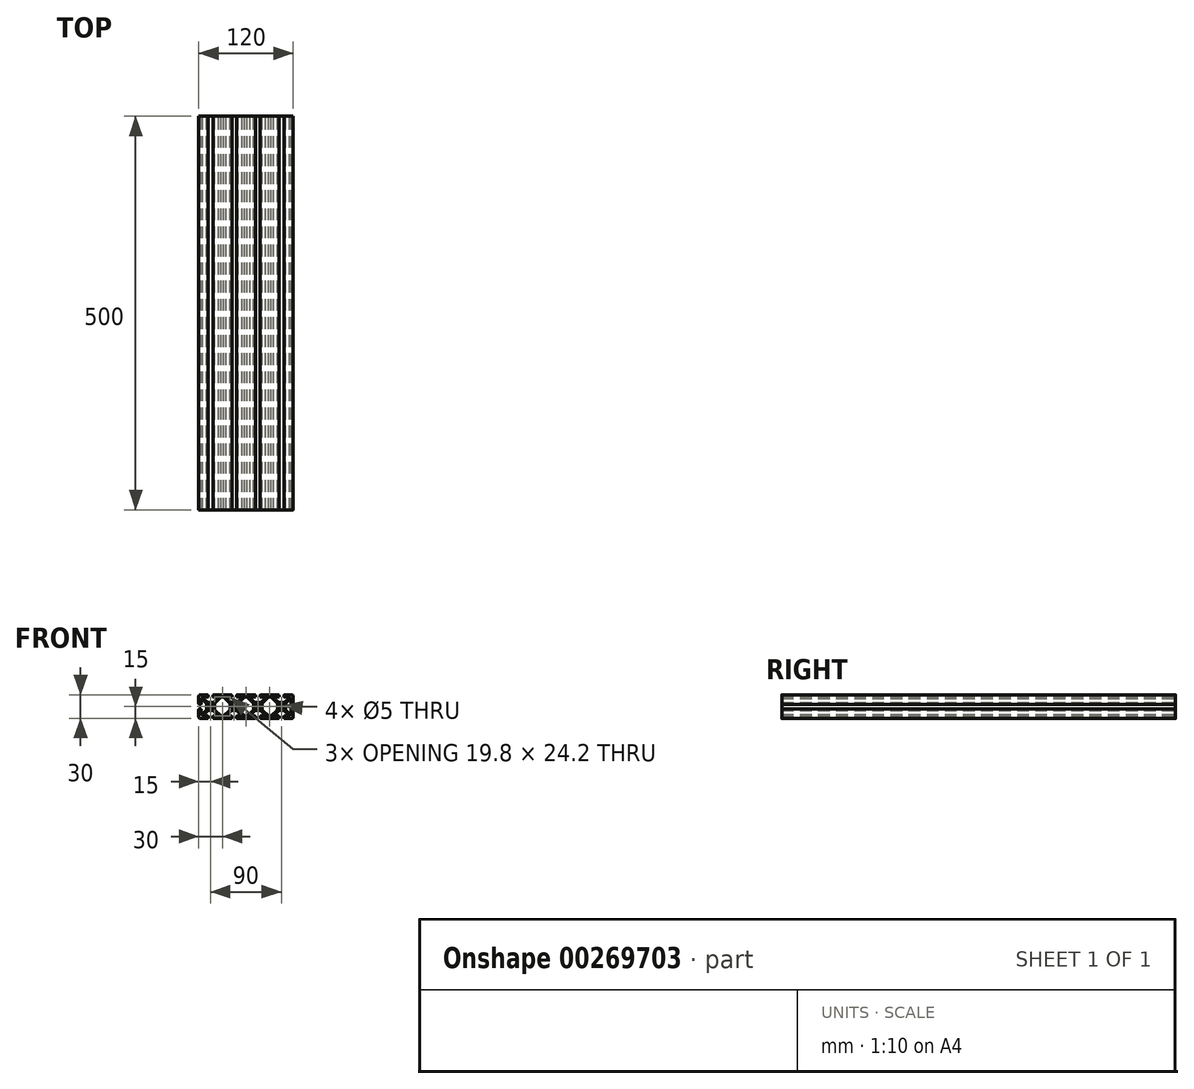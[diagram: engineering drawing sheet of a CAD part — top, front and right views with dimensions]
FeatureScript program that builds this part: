
annotation { "Feature Type Name" : "Feature", "Feature Type Description" : "" }
export const myFeature = defineFeature(function(context is Context, id is Id, definition is map)
    precondition{}
    {
        {
            var Q0;
            Q0=qCreatedBy(makeId("Front.planeOp"),FACE);
            var sketch = newSketch(context, id + "F0", { "sketchPlane" : qUnion([Q0])});
            skLineSegment(sketch, "E0.top", {"start": v(-58.2, -15) * mm, "end": v(-49, -15) * mm});
            skCircle(sketch, "E1", {"center": v(-45, 0) * mm, "radius": 2.5 * mm});
            skCircle(sketch, "E2", {"center": v(-15, 0) * mm, "radius": 2.5 * mm});
            skPoint(sketch, "E3", {"position": v(0, 10) * mm});
            skLineSegment(sketch, "E4", {"start": v(-45, 0) * mm, "end": v(-15, 0) * mm, "construction": true});
            skLineSegment(sketch, "E5", {"start": v(-15, 0) * mm, "end": v(0, 0) * mm, "construction": true});
            skPoint(sketch, "E6", {"position": v(0, 0) * mm});
            skLineSegment(sketch, "E7", {"start": v(-54.62, -12.1) * mm, "end": v(-48.5, -12.1) * mm});
            skLineSegment(sketch, "E8", {"start": v(-45, 0) * mm, "end": v(-45, -15) * mm, "construction": true});
            skLineSegment(sketch, "E9.bottom", {"start": v(-42.2, -5.1) * mm, "end": v(-47.8, -5.1) * mm});
            skLineSegment(sketch, "E10.trimOffspring", {"start": v(-48, -12.6) * mm, "end": v(-48, -14) * mm});
            skLineSegment(sketch, "E11.trimOffspring", {"start": v(-42, -12.6) * mm, "end": v(-42, -14) * mm});
            skLineSegment(sketch, "E12.trimOffspring", {"start": v(-41.5, -12.1) * mm, "end": v(-35.38, -12.1) * mm});
            skLineSegment(sketch, "E13.0", {"start": v(-56.25, -9.97) * mm, "end": v(-50.83, -4.56) * mm});
            skLineSegment(sketch, "E14.trimOffspring", {"start": v(-54.97, -11.25) * mm, "end": v(-49.56, -5.83) * mm});
            skLineSegment(sketch, "E15", {"start": v(-45, 0) * mm, "end": v(-60, -15) * mm, "construction": true});
            skLineSegment(sketch, "E16.MirrorCS", {"start": v(-57.1, -9.62) * mm, "end": v(-57.1, -3.5) * mm});
            skLineSegment(sketch, "E17.MirrorCS", {"start": v(-57.6, -3) * mm, "end": v(-59, -3) * mm});
            skLineSegment(sketch, "E18.MirrorCS", {"start": v(-35.03, -11.25) * mm, "end": v(-40.44, -5.83) * mm});
            skLineSegment(sketch, "E19.MirrorCS", {"start": v(-31.63, -12.1) * mm, "end": v(-39.17, -4.56) * mm});
            skLineSegment(sketch, "E20.trimOffspring", {"start": v(-60, -4) * mm, "end": v(-60, -13.2) * mm});
            skPoint(sketch, "E21.visualSharp", {"position": v(-60, -15) * mm});
            skArc(sketch, "E21.filletArc", {"start": v(-60, -13.2) * mm, "mid": v(-59.47, -14.47) * mm, "end": v(-58.2, -15) * mm});
            skPoint(sketch, "E22.visualSharp", {"position": v(-48, -15) * mm});
            skArc(sketch, "E22.filletArc", {"start": v(-49, -15) * mm, "mid": v(-48.3, -14.7) * mm, "end": v(-48, -14) * mm});
            skLineSegment(sketch, "E23", {"start": v(-48, -14) * mm, "end": v(-42, -14) * mm, "construction": true});
            skPoint(sketch, "E24", {"position": v(-45, -14) * mm});
            skPoint(sketch, "E25.orphan", {"position": v(-34.33, -5.1) * mm});
            skPoint(sketch, "E26.orphan", {"position": v(-45.67, -5.1) * mm});
            skPoint(sketch, "E27.visualSharp", {"position": v(-48.83, -5.1) * mm});
            skArc(sketch, "E27.filletArc", {"start": v(-47.8, -5.1) * mm, "mid": v(-48.75, -5.3) * mm, "end": v(-49.56, -5.83) * mm});
            skPoint(sketch, "E28.visualSharp", {"position": v(-41.17, -5.1) * mm});
            skArc(sketch, "E28.filletArc", {"start": v(-40.44, -5.83) * mm, "mid": v(-41.25, -5.3) * mm, "end": v(-42.2, -5.1) * mm});
            skPoint(sketch, "E29.visualSharp", {"position": v(-41.12, 5.15) * mm});
            skArc(sketch, "E29.filletArc", {"start": v(-50.83, -4.56) * mm, "mid": v(-50.3, -3.75) * mm, "end": v(-50.1, -2.8) * mm});
            skPoint(sketch, "E30.visualSharp", {"position": v(-48.88, 5.15) * mm});
            skPoint(sketch, "E31.visualSharp", {"position": v(-42, -15) * mm});
            skArc(sketch, "E31.filletArc", {"start": v(-42, -14) * mm, "mid": v(-41.7, -14.7) * mm, "end": v(-41, -15) * mm});
            skPoint(sketch, "E32.visualSharp", {"position": v(-42, -12.1) * mm});
            skArc(sketch, "E32.filletArc", {"start": v(-41.5, -12.1) * mm, "mid": v(-41.85, -12.25) * mm, "end": v(-42, -12.6) * mm});
            skPoint(sketch, "E33.visualSharp", {"position": v(-48, -12.1) * mm});
            skArc(sketch, "E33.filletArc", {"start": v(-48, -12.6) * mm, "mid": v(-48.15, -12.25) * mm, "end": v(-48.5, -12.1) * mm});
            skPoint(sketch, "E34.visualSharp", {"position": v(-57.1, -3) * mm});
            skArc(sketch, "E34.filletArc", {"start": v(-57.1, -3.5) * mm, "mid": v(-57.25, -3.15) * mm, "end": v(-57.6, -3) * mm});
            skPoint(sketch, "E35.visualSharp", {"position": v(-60, -3) * mm});
            skArc(sketch, "E35.filletArc", {"start": v(-59, -3) * mm, "mid": v(-59.7, -3.3) * mm, "end": v(-60, -4) * mm});
            skPoint(sketch, "E36.visualSharp", {"position": v(-57.1, -10.83) * mm});
            skArc(sketch, "E36.filletArc", {"start": v(-57.1, -9.62) * mm, "mid": v(-56.8, -10.08) * mm, "end": v(-56.25, -9.97) * mm});
            skPoint(sketch, "E37.visualSharp", {"position": v(-55.83, -12.1) * mm});
            skArc(sketch, "E37.filletArc", {"start": v(-54.97, -11.25) * mm, "mid": v(-55.08, -11.8) * mm, "end": v(-54.62, -12.1) * mm});
            skPoint(sketch, "E38.visualSharp", {"position": v(-34.17, -12.1) * mm});
            skArc(sketch, "E38.filletArc", {"start": v(-35.38, -12.1) * mm, "mid": v(-34.92, -11.8) * mm, "end": v(-35.03, -11.25) * mm});
            skLineSegment(sketch, "E39", {"start": v(-43.9, 2.36) * mm, "end": v(-42.64, 1.1) * mm, "construction": true});
            skPoint(sketch, "E40", {"position": v(-43.27, 1.73) * mm});
            skLineSegment(sketch, "E41.MirrorCS", {"start": v(-58.2, 15) * mm, "end": v(-49, 15) * mm});
            skArc(sketch, "E42.MirrorCS", {"start": v(-60, 13.2) * mm, "mid": v(-59.47, 14.47) * mm, "end": v(-58.2, 15) * mm});
            skLineSegment(sketch, "E43.MirrorCS", {"start": v(-60, 4) * mm, "end": v(-60, 13.2) * mm});
            skArc(sketch, "E44.MirrorCS", {"start": v(-59, 3) * mm, "mid": v(-59.7, 3.3) * mm, "end": v(-60, 4) * mm});
            skLineSegment(sketch, "E45.MirrorCS", {"start": v(-57.6, 3) * mm, "end": v(-59, 3) * mm});
            skArc(sketch, "E46.MirrorCS", {"start": v(-57.1, 3.5) * mm, "mid": v(-57.25, 3.15) * mm, "end": v(-57.6, 3) * mm});
            skLineSegment(sketch, "E47.MirrorCS", {"start": v(-57.1, 9.62) * mm, "end": v(-57.1, 3.5) * mm});
            skArc(sketch, "E48.MirrorCS", {"start": v(-57.1, 9.62) * mm, "mid": v(-56.8, 10.08) * mm, "end": v(-56.25, 9.97) * mm});
            skLineSegment(sketch, "E49.MirrorCS", {"start": v(-56.25, 9.97) * mm, "end": v(-50.83, 4.56) * mm});
            skArc(sketch, "E50.MirrorCS", {"start": v(-50.83, 4.56) * mm, "mid": v(-50.3, 3.75) * mm, "end": v(-50.1, 2.8) * mm});
            skArc(sketch, "E51.MirrorCS", {"start": v(-49, 15) * mm, "mid": v(-48.3, 14.7) * mm, "end": v(-48, 14) * mm});
            skLineSegment(sketch, "E52.MirrorCS", {"start": v(-48, 12.6) * mm, "end": v(-48, 14) * mm});
            skArc(sketch, "E53.MirrorCS", {"start": v(-48, 12.6) * mm, "mid": v(-48.15, 12.25) * mm, "end": v(-48.5, 12.1) * mm});
            skLineSegment(sketch, "E54.MirrorCS", {"start": v(-54.62, 12.1) * mm, "end": v(-48.5, 12.1) * mm});
            skArc(sketch, "E55.MirrorCS", {"start": v(-54.97, 11.25) * mm, "mid": v(-55.08, 11.8) * mm, "end": v(-54.62, 12.1) * mm});
            skLineSegment(sketch, "E56.MirrorCS", {"start": v(-54.97, 11.25) * mm, "end": v(-49.56, 5.83) * mm});
            skArc(sketch, "E57.MirrorCS", {"start": v(-47.8, 5.1) * mm, "mid": v(-48.75, 5.3) * mm, "end": v(-49.56, 5.83) * mm});
            skLineSegment(sketch, "E58.MirrorCS", {"start": v(-42.2, 5.1) * mm, "end": v(-47.8, 5.1) * mm});
            skArc(sketch, "E59.MirrorCS", {"start": v(-40.44, 5.83) * mm, "mid": v(-41.25, 5.3) * mm, "end": v(-42.2, 5.1) * mm});
            skLineSegment(sketch, "E60.MirrorCS", {"start": v(-35.03, 11.25) * mm, "end": v(-40.44, 5.83) * mm});
            skArc(sketch, "E61.MirrorCS", {"start": v(-35.38, 12.1) * mm, "mid": v(-34.92, 11.8) * mm, "end": v(-35.03, 11.25) * mm});
            skLineSegment(sketch, "E62.MirrorCS", {"start": v(-41.5, 12.1) * mm, "end": v(-35.38, 12.1) * mm});
            skArc(sketch, "E63.MirrorCS", {"start": v(-41.5, 12.1) * mm, "mid": v(-41.85, 12.25) * mm, "end": v(-42, 12.6) * mm});
            skLineSegment(sketch, "E64.MirrorCS", {"start": v(-42, 12.6) * mm, "end": v(-42, 14) * mm});
            skArc(sketch, "E65.MirrorCS", {"start": v(-42, 14) * mm, "mid": v(-41.7, 14.7) * mm, "end": v(-41, 15) * mm});
            skLineSegment(sketch, "E66.MirrorCS", {"start": v(-31.63, 12.1) * mm, "end": v(-39.17, 4.56) * mm});
            skLineSegment(sketch, "E67", {"start": v(-50.1, -2.8) * mm, "end": v(-50.1, 2.8) * mm});
            skLineSegment(sketch, "E68", {"start": v(-39.9, 2.8) * mm, "end": v(-39.9, -2.8) * mm});
            skLineSegment(sketch, "E69", {"start": v(-30, 0) * mm, "end": v(-30, -12.6) * mm, "construction": true});
            skLineSegment(sketch, "E70.MirrorCS", {"start": v(-18, -12.6) * mm, "end": v(-18, -14) * mm});
            skArc(sketch, "E71.MirrorCS", {"start": v(-18.5, -12.1) * mm, "mid": v(-18.15, -12.25) * mm, "end": v(-18, -12.6) * mm});
            skPoint(sketch, "E72.MirrorP", {"position": v(-18, -15) * mm});
            skArc(sketch, "E73.MirrorCS", {"start": v(-18, -14) * mm, "mid": v(-18.3, -14.7) * mm, "end": v(-19, -15) * mm});
            skPoint(sketch, "E74.MirrorP", {"position": v(-18, -12.1) * mm});
            skLineSegment(sketch, "E75.MirrorCS", {"start": v(-18.5, -12.1) * mm, "end": v(-24.62, -12.1) * mm});
            skPoint(sketch, "E76.MirrorP", {"position": v(-25.83, -12.1) * mm});
            skPoint(sketch, "E77.MirrorP", {"position": v(-11.12, 5.15) * mm});
            skPoint(sketch, "E78.MirrorP", {"position": v(-14.33, -5.1) * mm});
            skPoint(sketch, "E79.MirrorP", {"position": v(-18.83, -5.1) * mm});
            skLineSegment(sketch, "E80.MirrorCS", {"start": v(-28.37, -12.1) * mm, "end": v(-20.83, -4.56) * mm});
            skLineSegment(sketch, "E81.MirrorCS", {"start": v(-18, 12.6) * mm, "end": v(-18, 14) * mm});
            skArc(sketch, "E82.MirrorCS", {"start": v(-18, 14) * mm, "mid": v(-18.3, 14.7) * mm, "end": v(-19, 15) * mm});
            skLineSegment(sketch, "E83.MirrorCS", {"start": v(-24.97, 11.25) * mm, "end": v(-19.56, 5.83) * mm});
            skLineSegment(sketch, "E84.MirrorCS", {"start": v(-28.37, 12.1) * mm, "end": v(-20.83, 4.56) * mm});
            skLineSegment(sketch, "E85.MirrorCS", {"start": v(-18.5, 12.1) * mm, "end": v(-24.62, 12.1) * mm});
            skArc(sketch, "E86.MirrorCS", {"start": v(-18.5, 12.1) * mm, "mid": v(-18.15, 12.25) * mm, "end": v(-18, 12.6) * mm});
            skArc(sketch, "E87.MirrorCS", {"start": v(-24.62, 12.1) * mm, "mid": v(-25.08, 11.8) * mm, "end": v(-24.97, 11.25) * mm});
            skArc(sketch, "E88.MirrorCS", {"start": v(-19.56, 5.83) * mm, "mid": v(-18.75, 5.3) * mm, "end": v(-17.8, 5.1) * mm});
            skLineSegment(sketch, "E89.MirrorCS", {"start": v(-17.8, 5.1) * mm, "end": v(-12.2, 5.1) * mm});
            skArc(sketch, "E90.MirrorCS", {"start": v(-11, -15) * mm, "mid": v(-11.7, -14.7) * mm, "end": v(-12, -14) * mm});
            skLineSegment(sketch, "E91.MirrorCS", {"start": v(-12, -12.6) * mm, "end": v(-12, -14) * mm});
            skArc(sketch, "E92.MirrorCS", {"start": v(-12, -12.6) * mm, "mid": v(-11.85, -12.25) * mm, "end": v(-11.5, -12.1) * mm});
            skLineSegment(sketch, "E93.MirrorCS", {"start": v(-5.38, -12.1) * mm, "end": v(-11.5, -12.1) * mm});
            skPoint(sketch, "E94.visualSharp", {"position": v(-31.63, 12.1) * mm});
            skPoint(sketch, "E95.visualSharp", {"position": v(-28.37, 12.1) * mm});
            skPoint(sketch, "E96.visualSharp", {"position": v(-31.63, -12.1) * mm});
            skPoint(sketch, "E97.visualSharp", {"position": v(-28.37, -12.1) * mm});
            skArc(sketch, "E98.MirrorCS", {"start": v(-24.62, -12.1) * mm, "mid": v(-25.08, -11.8) * mm, "end": v(-24.97, -11.25) * mm});
            skLineSegment(sketch, "E99.MirrorCS", {"start": v(-24.97, -11.25) * mm, "end": v(-19.56, -5.83) * mm});
            skArc(sketch, "E100.MirrorCS", {"start": v(-19.56, -5.83) * mm, "mid": v(-18.75, -5.3) * mm, "end": v(-17.8, -5.1) * mm});
            skLineSegment(sketch, "E101.MirrorCS", {"start": v(-17.8, -5.1) * mm, "end": v(-12.2, -5.1) * mm});
            skArc(sketch, "E102.MirrorCS", {"start": v(-12.2, -5.1) * mm, "mid": v(-11.25, -5.3) * mm, "end": v(-10.44, -5.83) * mm});
            skLineSegment(sketch, "E103.MirrorCS", {"start": v(-5.03, -11.25) * mm, "end": v(-10.44, -5.83) * mm});
            skArc(sketch, "E104.MirrorCS", {"start": v(-5.03, -11.25) * mm, "mid": v(-4.92, -11.8) * mm, "end": v(-5.38, -12.1) * mm});
            skArc(sketch, "E105.MirrorCS", {"start": v(-12.2, 5.1) * mm, "mid": v(-11.25, 5.3) * mm, "end": v(-10.44, 5.83) * mm});
            skLineSegment(sketch, "E106.MirrorCS", {"start": v(-5.03, 11.25) * mm, "end": v(-10.44, 5.83) * mm});
            skArc(sketch, "E107.MirrorCS", {"start": v(-5.03, 11.25) * mm, "mid": v(-4.92, 11.8) * mm, "end": v(-5.38, 12.1) * mm});
            skLineSegment(sketch, "E108.MirrorCS", {"start": v(-5.38, 12.1) * mm, "end": v(-11.5, 12.1) * mm});
            skArc(sketch, "E109.MirrorCS", {"start": v(-12, 12.6) * mm, "mid": v(-11.85, 12.25) * mm, "end": v(-11.5, 12.1) * mm});
            skLineSegment(sketch, "E110.MirrorCS", {"start": v(-12, 12.6) * mm, "end": v(-12, 14) * mm});
            skArc(sketch, "E111.MirrorCS", {"start": v(-11, 15) * mm, "mid": v(-11.7, 14.7) * mm, "end": v(-12, 14) * mm});
            skArc(sketch, "E112.MirrorCS", {"start": v(-9.17, -4.56) * mm, "mid": v(-9.7, -3.75) * mm, "end": v(-9.9, -2.8) * mm});
            skLineSegment(sketch, "E113.MirrorCS", {"start": v(-9.9, -2.8) * mm, "end": v(-9.9, 2.8) * mm});
            skArc(sketch, "E114.MirrorCS", {"start": v(-9.17, 4.56) * mm, "mid": v(-9.7, 3.75) * mm, "end": v(-9.9, 2.8) * mm});
            skLineSegment(sketch, "E115", {"start": v(-15, 0) * mm, "end": v(-15, -13.35) * mm, "construction": true});
            skLineSegment(sketch, "E116", {"start": v(-41, -15) * mm, "end": v(-30, -15) * mm});
            skLineSegment(sketch, "E117", {"start": v(-30, -15) * mm, "end": v(-19, -15) * mm});
            skLineSegment(sketch, "E118.MirrorCS", {"start": v(-30, 15) * mm, "end": v(-19, 15) * mm});
            skLineSegment(sketch, "E119.MirrorCS", {"start": v(-41, 15) * mm, "end": v(-30, 15) * mm});
            skLineSegment(sketch, "E120.MirrorCS", {"start": v(0, -15) * mm, "end": v(-11, -15) * mm});
            skLineSegment(sketch, "E121.MirrorCS", {"start": v(-1.63, -12.1) * mm, "end": v(-9.9, -3.83) * mm});
            skLineSegment(sketch, "E122.MirrorCS", {"start": v(0, -12.1) * mm, "end": v(-1.63, -12.1) * mm});
            skLineSegment(sketch, "E123.MirrorCS", {"start": v(0, 15) * mm, "end": v(-11, 15) * mm});
            skLineSegment(sketch, "E124.MirrorCS", {"start": v(-1.63, 12.1) * mm, "end": v(-9.9, 3.83) * mm});
            skLineSegment(sketch, "E125", {"start": v(0, 10) * mm, "end": v(0, -15) * mm, "construction": true});
            skPoint(sketch, "E126.orphan", {"position": v(15, 0) * mm});
            skLineSegment(sketch, "E127", {"start": v(0, -15) * mm, "end": v(0, -12.1) * mm});
            skLineSegment(sketch, "E128", {"start": v(0, 15) * mm, "end": v(0, 12.1) * mm});
            skLineSegment(sketch, "E129", {"start": v(-31.63, 12.1) * mm, "end": v(-28.37, 12.1) * mm});
            skLineSegment(sketch, "E130", {"start": v(-31.63, -12.1) * mm, "end": v(-28.37, -12.1) * mm});
            skLineSegment(sketch, "E131", {"start": v(-1.63, 12.1) * mm, "end": v(0, 12.1) * mm});
            skPoint(sketch, "E132.visualSharp", {"position": v(-39.9, 3.83) * mm});
            skArc(sketch, "E132.filletArc", {"start": v(-39.17, 4.56) * mm, "mid": v(-39.7, 3.75) * mm, "end": v(-39.9, 2.8) * mm});
            skPoint(sketch, "E133.visualSharp", {"position": v(-39.9, -3.83) * mm});
            skArc(sketch, "E133.filletArc", {"start": v(-39.9, -2.8) * mm, "mid": v(-39.7, -3.75) * mm, "end": v(-39.17, -4.56) * mm});
            skPoint(sketch, "E134.visualSharp", {"position": v(-20.1, 3.83) * mm});
            skArc(sketch, "E134.filletArc", {"start": v(-20.1, 2.8) * mm, "mid": v(-20.3, 3.75) * mm, "end": v(-20.83, 4.56) * mm});
            skLineSegment(sketch, "E135", {"start": v(-20.1, 2.8) * mm, "end": v(-20.1, -2.8) * mm});
            skPoint(sketch, "E136.visualSharp", {"position": v(-20.1, -3.83) * mm});
            skArc(sketch, "E136.filletArc", {"start": v(-20.83, -4.56) * mm, "mid": v(-20.3, -3.75) * mm, "end": v(-20.1, -2.8) * mm});
            skSolve(sketch);
        }
        {
            var Q0;
            Q0=makeQuery(id+"F0.imprint","IMPRINT",FACE,{"disambiguationData":[TD([[makeQuery(id+"F0.imprint","IMPRINT",EDGE,{"derivedFrom":sQuery(id+"F0.wireOp",EDGE,"E0.top")}),1.0]])]});
            extrude(context, id + "F1", {"entities" : qUnion([Q0]), "depth" : 500 * mm});
        }
        {
            var Q0;
            Q0=makeQuery(id+"F1.opExtrude","SWEPT_BODY",BODY,{"disambiguationData":[OSD([sQuery(id+"F0.wireOp",EDGE,"E0.top"),sQuery(id+"F0.wireOp",EDGE,"E1"),sQuery(id+"F0.wireOp",EDGE,"E2"),sQuery(id+"F0.wireOp",EDGE,"E7"),sQuery(id+"F0.wireOp",EDGE,"E9.bottom"),sQuery(id+"F0.wireOp",EDGE,"E10.trimOffspring"),sQuery(id+"F0.wireOp",EDGE,"E11.trimOffspring"),sQuery(id+"F0.wireOp",EDGE,"E12.trimOffspring"),sQuery(id+"F0.wireOp",EDGE,"E13.0"),sQuery(id+"F0.wireOp",EDGE,"E14.trimOffspring"),sQuery(id+"F0.wireOp",EDGE,"E16.MirrorCS"),sQuery(id+"F0.wireOp",EDGE,"E17.MirrorCS"),sQuery(id+"F0.wireOp",EDGE,"E18.MirrorCS"),sQuery(id+"F0.wireOp",EDGE,"E19.MirrorCS"),sQuery(id+"F0.wireOp",EDGE,"E20.trimOffspring"),sQuery(id+"F0.wireOp",EDGE,"E21.filletArc"),sQuery(id+"F0.wireOp",EDGE,"E22.filletArc"),sQuery(id+"F0.wireOp",EDGE,"E27.filletArc"),sQuery(id+"F0.wireOp",EDGE,"E28.filletArc"),sQuery(id+"F0.wireOp",EDGE,"E29.filletArc"),sQuery(id+"F0.wireOp",EDGE,"E30.filletArc"),sQuery(id+"F0.wireOp",EDGE,"E31.filletArc"),sQuery(id+"F0.wireOp",EDGE,"E32.filletArc"),sQuery(id+"F0.wireOp",EDGE,"E33.filletArc"),sQuery(id+"F0.wireOp",EDGE,"E34.filletArc"),sQuery(id+"F0.wireOp",EDGE,"E35.filletArc"),sQuery(id+"F0.wireOp",EDGE,"E36.filletArc"),sQuery(id+"F0.wireOp",EDGE,"E37.filletArc"),sQuery(id+"F0.wireOp",EDGE,"E38.filletArc"),sQuery(id+"F0.wireOp",EDGE,"E41.MirrorCS"),sQuery(id+"F0.wireOp",EDGE,"E42.MirrorCS"),sQuery(id+"F0.wireOp",EDGE,"E43.MirrorCS"),sQuery(id+"F0.wireOp",EDGE,"E44.MirrorCS"),sQuery(id+"F0.wireOp",EDGE,"E45.MirrorCS"),sQuery(id+"F0.wireOp",EDGE,"E46.MirrorCS"),sQuery(id+"F0.wireOp",EDGE,"E47.MirrorCS"),sQuery(id+"F0.wireOp",EDGE,"E48.MirrorCS"),sQuery(id+"F0.wireOp",EDGE,"E49.MirrorCS"),sQuery(id+"F0.wireOp",EDGE,"E50.MirrorCS"),sQuery(id+"F0.wireOp",EDGE,"E51.MirrorCS"),sQuery(id+"F0.wireOp",EDGE,"E52.MirrorCS"),sQuery(id+"F0.wireOp",EDGE,"E53.MirrorCS"),sQuery(id+"F0.wireOp",EDGE,"E54.MirrorCS"),sQuery(id+"F0.wireOp",EDGE,"E55.MirrorCS"),sQuery(id+"F0.wireOp",EDGE,"E56.MirrorCS"),sQuery(id+"F0.wireOp",EDGE,"E57.MirrorCS"),sQuery(id+"F0.wireOp",EDGE,"E58.MirrorCS"),sQuery(id+"F0.wireOp",EDGE,"E59.MirrorCS"),sQuery(id+"F0.wireOp",EDGE,"E60.MirrorCS"),sQuery(id+"F0.wireOp",EDGE,"E61.MirrorCS"),sQuery(id+"F0.wireOp",EDGE,"E62.MirrorCS"),sQuery(id+"F0.wireOp",EDGE,"E63.MirrorCS"),sQuery(id+"F0.wireOp",EDGE,"E64.MirrorCS"),sQuery(id+"F0.wireOp",EDGE,"E65.MirrorCS"),sQuery(id+"F0.wireOp",EDGE,"E66.MirrorCS"),sQuery(id+"F0.wireOp",EDGE,"84e0606f-2660-47d3-8066-1f6780e61d240.MirrorCS"),sQuery(id+"F0.wireOp",EDGE,"E67"),sQuery(id+"F0.wireOp",EDGE,"E68"),sQuery(id+"F0.wireOp",EDGE,"E70.MirrorCS"),sQuery(id+"F0.wireOp",EDGE,"E71.MirrorCS"),sQuery(id+"F0.wireOp",EDGE,"E73.MirrorCS"),sQuery(id+"F0.wireOp",EDGE,"E75.MirrorCS"),sQuery(id+"F0.wireOp",EDGE,"2eeeb882-eed5-4166-8e1e-a32fedb74f402.MirrorCS"),sQuery(id+"F0.wireOp",EDGE,"2eeeb882-eed5-4166-8e1e-a32fedb74f404.MirrorCS"),sQuery(id+"F0.wireOp",EDGE,"E80.MirrorCS"),sQuery(id+"F0.wireOp",EDGE,"E81.MirrorCS"),sQuery(id+"F0.wireOp",EDGE,"E82.MirrorCS"),sQuery(id+"F0.wireOp",EDGE,"E83.MirrorCS"),sQuery(id+"F0.wireOp",EDGE,"E84.MirrorCS"),sQuery(id+"F0.wireOp",EDGE,"E85.MirrorCS"),sQuery(id+"F0.wireOp",EDGE,"E86.MirrorCS"),sQuery(id+"F0.wireOp",EDGE,"E87.MirrorCS"),sQuery(id+"F0.wireOp",EDGE,"E88.MirrorCS"),sQuery(id+"F0.wireOp",EDGE,"c75a34bd-beff-4123-8e26-f2b4586136f20.MirrorCS"),sQuery(id+"F0.wireOp",EDGE,"E89.MirrorCS"),sQuery(id+"F0.wireOp",EDGE,"E90.MirrorCS"),sQuery(id+"F0.wireOp",EDGE,"E91.MirrorCS"),sQuery(id+"F0.wireOp",EDGE,"E92.MirrorCS"),sQuery(id+"F0.wireOp",EDGE,"E93.MirrorCS"),sQuery(id+"F0.wireOp",EDGE,"NHzEeUZn-j6aY-zjJj-DU6j-r29A23V1wuZp"),sQuery(id+"F0.wireOp",EDGE,"euIQqrrk-acdu-msLV-AXC1-f6gACNh7W0Cw"),sQuery(id+"F0.wireOp",EDGE,"E94.filletArc"),sQuery(id+"F0.wireOp",EDGE,"E95.filletArc"),sQuery(id+"F0.wireOp",EDGE,"E96.filletArc"),sQuery(id+"F0.wireOp",EDGE,"E97.filletArc"),sQuery(id+"F0.wireOp",EDGE,"E98.MirrorCS"),sQuery(id+"F0.wireOp",EDGE,"E99.MirrorCS"),sQuery(id+"F0.wireOp",EDGE,"E100.MirrorCS"),sQuery(id+"F0.wireOp",EDGE,"E101.MirrorCS"),sQuery(id+"F0.wireOp",EDGE,"E102.MirrorCS"),sQuery(id+"F0.wireOp",EDGE,"E103.MirrorCS"),sQuery(id+"F0.wireOp",EDGE,"E104.MirrorCS"),sQuery(id+"F0.wireOp",EDGE,"E105.MirrorCS"),sQuery(id+"F0.wireOp",EDGE,"E106.MirrorCS"),sQuery(id+"F0.wireOp",EDGE,"E107.MirrorCS"),sQuery(id+"F0.wireOp",EDGE,"E108.MirrorCS"),sQuery(id+"F0.wireOp",EDGE,"E109.MirrorCS"),sQuery(id+"F0.wireOp",EDGE,"E110.MirrorCS"),sQuery(id+"F0.wireOp",EDGE,"E111.MirrorCS"),sQuery(id+"F0.wireOp",EDGE,"E112.MirrorCS"),sQuery(id+"F0.wireOp",EDGE,"E113.MirrorCS"),sQuery(id+"F0.wireOp",EDGE,"E114.MirrorCS"),sQuery(id+"F0.wireOp",EDGE,"E116"),sQuery(id+"F0.wireOp",EDGE,"E117"),sQuery(id+"F0.wireOp",EDGE,"E118.MirrorCS"),sQuery(id+"F0.wireOp",EDGE,"E119.MirrorCS"),sQuery(id+"F0.wireOp",EDGE,"E120.MirrorCS"),sQuery(id+"F0.wireOp",EDGE,"E121.MirrorCS"),sQuery(id+"F0.wireOp",EDGE,"095b0e8a-5b2c-452e-882b-1944bbcbc7fe0.MirrorCS"),sQuery(id+"F0.wireOp",EDGE,"E122.MirrorCS"),sQuery(id+"F0.wireOp",EDGE,"E123.MirrorCS"),sQuery(id+"F0.wireOp",EDGE,"E124.MirrorCS"),sQuery(id+"F0.wireOp",EDGE,"0347e20a-31d5-45e7-a402-947e340792340.MirrorCS"),sQuery(id+"F0.wireOp",EDGE,"5deaee7e-06ea-4911-bed0-68f2c0d7f7c50.MirrorCS"),sQuery(id+"F0.wireOp",EDGE,"zOQuU1W7-kDfO-8kRA-MtJh-F7DlEQ6mTgwY"),sQuery(id+"F0.wireOp",EDGE,"E127")])]});
            var Q1;
            Q1=qCreatedBy(makeId("Right.planeOp"),FACE);
            mirror(context, id + "F2", {"operationType" : NewBodyOperationType.ADD, "entities" : qUnion([Q0]), "mirrorPlane" : qUnion([Q1])});
        }
    });
